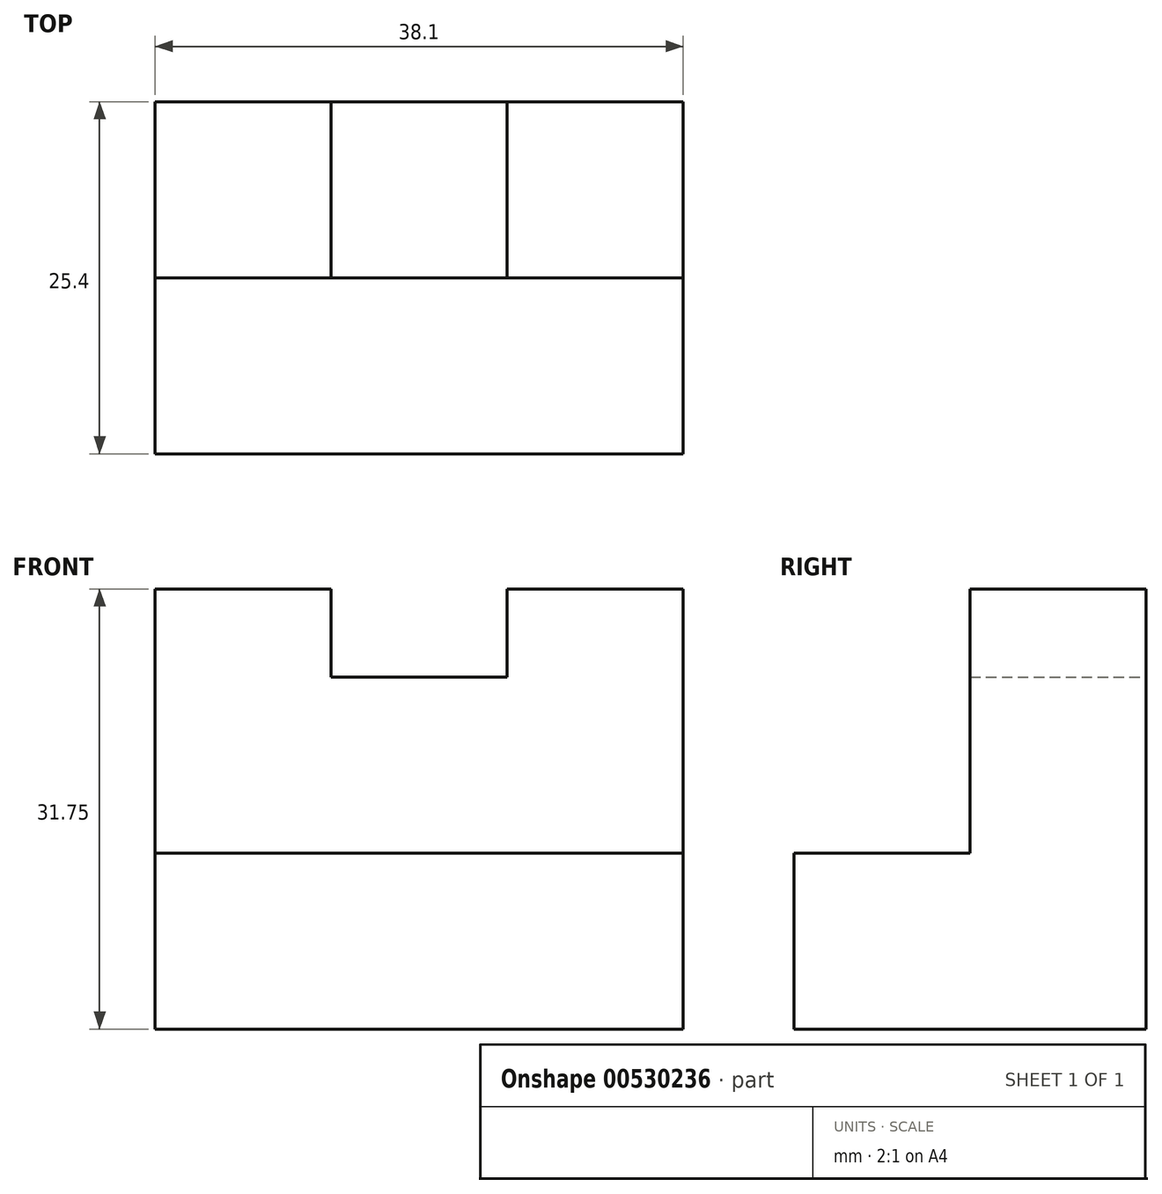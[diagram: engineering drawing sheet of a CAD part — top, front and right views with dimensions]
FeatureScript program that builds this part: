
annotation { "Feature Type Name" : "Feature", "Feature Type Description" : "" }
export const myFeature = defineFeature(function(context is Context, id is Id, definition is map)
    precondition{}
    {
        {
            var Q0;
            Q0=qCreatedBy(makeId("Front.planeOp"),FACE);
            var sketch = newSketch(context, id + "F0", { "sketchPlane" : qUnion([Q0])});
            skLineSegment(sketch, "E0.bottom", {"start": v(-51.36, 12.7) * mm, "end": v(-13.26, 12.7) * mm});
            skLineSegment(sketch, "E0.top", {"start": v(-51.36, 0) * mm, "end": v(-13.26, 0) * mm});
            skLineSegment(sketch, "E0.left", {"start": v(-51.36, 12.7) * mm, "end": v(-51.36, 0) * mm});
            skLineSegment(sketch, "E0.right", {"start": v(-13.26, 12.7) * mm, "end": v(-13.26, 0) * mm});
            skSolve(sketch);
        }
        {
            var Q0;
            Q0 = qSketchRegion(id + "F0", true);
            extrude(context, id + "F1", {"entities" : qUnion([Q0]), "depth" : 25.4 * mm, "offsetDistance" : 25.4 * mm});
        }
        {
            var Q0;
            Q0=makeQuery(id+"F1.opExtrude","CAP_FACE",FACE,{"disambiguationData":[OSD([sQuery(id+"F0.wireOp",EDGE,"E0.bottom"),sQuery(id+"F0.wireOp",EDGE,"E0.top"),sQuery(id+"F0.wireOp",EDGE,"E0.left"),sQuery(id+"F0.wireOp",EDGE,"E0.right")])],"isStart":true});
            var sketch = newSketch(context, id + "F2", { "sketchPlane" : qUnion([Q0])});
            skLineSegment(sketch, "E1.bottom", {"start": v(13.26, 12.7) * mm, "end": v(51.36, 12.7) * mm});
            skLineSegment(sketch, "E1.top", {"start": v(13.26, 31.75) * mm, "end": v(51.36, 31.75) * mm});
            skLineSegment(sketch, "E1.left", {"start": v(13.26, 12.7) * mm, "end": v(13.26, 31.75) * mm});
            skLineSegment(sketch, "E1.right", {"start": v(51.36, 12.7) * mm, "end": v(51.36, 31.75) * mm});
            skSolve(sketch);
        }
        {
            var Q0;
            Q0 = qSketchRegion(id + "F2", true);
            extrude(context, id + "F3", {"entities" : qUnion([Q0]), "operationType" : NewBodyOperationType.ADD, "oppositeDirection" : true, "depth" : 12.7 * mm, "offsetDistance" : 25.4 * mm});
        }
        {
            var Q0;
            Q0=makeQuery(id+"F3.boolean.opBoolean","MERGE",FACE,{"derivedFrom":[makeQuery(id+"F1.opExtrude","CAP_FACE",FACE,{"disambiguationData":[OSD([sQuery(id+"F0.wireOp",EDGE,"E0.bottom"),sQuery(id+"F0.wireOp",EDGE,"E0.top"),sQuery(id+"F0.wireOp",EDGE,"E0.left"),sQuery(id+"F0.wireOp",EDGE,"E0.right")])],"isStart":true}),makeQuery(id+"F3.opExtrude","CAP_FACE",FACE,{"disambiguationData":[OSD([sQuery(id+"F2.wireOp",EDGE,"E1.bottom"),sQuery(id+"F2.wireOp",EDGE,"E1.top"),sQuery(id+"F2.wireOp",EDGE,"E1.left"),sQuery(id+"F2.wireOp",EDGE,"E1.right")])],"isStart":true})]});
            var sketch = newSketch(context, id + "F4", { "sketchPlane" : qUnion([Q0])});
            skLineSegment(sketch, "E2", {"start": v(25.96, 31.75) * mm, "end": v(25.96, 25.4) * mm});
            skLineSegment(sketch, "E3", {"start": v(25.96, 25.4) * mm, "end": v(38.66, 25.4) * mm});
            skLineSegment(sketch, "E4", {"start": v(38.66, 25.4) * mm, "end": v(38.66, 31.75) * mm});
            skLineSegment(sketch, "E5", {"start": v(38.66, 31.75) * mm, "end": v(25.96, 31.75) * mm});
            skSolve(sketch);
        }
        {
            var Q0;
            Q0 = qSketchRegion(id + "F4", true);
            extrude(context, id + "F5", {"entities" : qUnion([Q0]), "operationType" : NewBodyOperationType.REMOVE, "oppositeDirection" : true, "depth" : 25.4 * mm, "offsetDistance" : 25.4 * mm});
        }
    });
